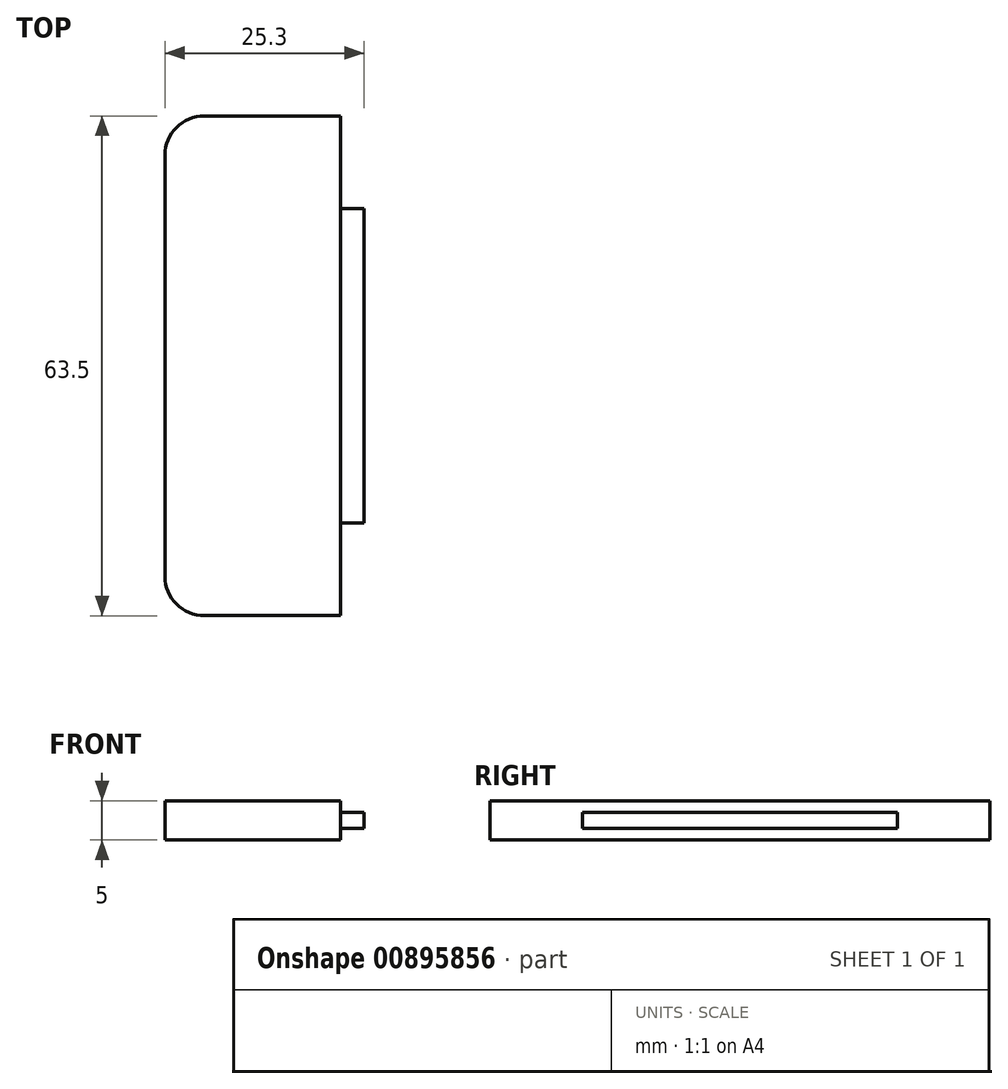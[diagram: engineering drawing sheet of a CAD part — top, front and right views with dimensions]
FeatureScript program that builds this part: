
annotation { "Feature Type Name" : "Feature", "Feature Type Description" : "" }
export const myFeature = defineFeature(function(context is Context, id is Id, definition is map)
    precondition{}
    {
        {
            var Q0;
            Q0=qCreatedBy(makeId("Right.planeOp"),FACE);
            var sketch = newSketch(context, id + "F0", { "sketchPlane" : qUnion([Q0])});
            skLineSegment(sketch, "E0.bottom", {"start": v(-31.75, 0) * mm, "end": v(31.75, 0) * mm});
            skLineSegment(sketch, "E0.top", {"start": v(-31.75, 5) * mm, "end": v(31.75, 5) * mm});
            skLineSegment(sketch, "E0.left", {"start": v(-31.75, 0) * mm, "end": v(-31.75, 5) * mm});
            skLineSegment(sketch, "E0.right", {"start": v(31.75, 0) * mm, "end": v(31.75, 5) * mm});
            skSolve(sketch);
        }
        {
            var Q0;
            Q0=makeQuery(id+"F0.imprint","IMPRINT",FACE,{"disambiguationData":[TD([[makeQuery(id+"F0.imprint","IMPRINT",EDGE,{"derivedFrom":sQuery(id+"F0.wireOp",EDGE,"E0.bottom")}),1.0]])]});
            extrude(context, id + "F1", {"entities" : qUnion([Q0]), "oppositeDirection" : true, "depth" : 22.3 * mm, "offsetDistance" : 25 * mm});
        }
        {
            var Q0;
            Q0=makeQuery(id+"F1.opExtrude","CAP_FACE",FACE,{"disambiguationData":[OSD([sQuery(id+"F0.wireOp",EDGE,"E0.bottom"),sQuery(id+"F0.wireOp",EDGE,"E0.top"),sQuery(id+"F0.wireOp",EDGE,"E0.left"),sQuery(id+"F0.wireOp",EDGE,"E0.right")])],"isStart":true});
            var sketch = newSketch(context, id + "F2", { "sketchPlane" : qUnion([Q0])});
            skLineSegment(sketch, "E1.bottom", {"start": v(-20, 1.5) * mm, "end": v(20, 1.5) * mm});
            skLineSegment(sketch, "E1.top", {"start": v(-20, 3.5) * mm, "end": v(20, 3.5) * mm});
            skLineSegment(sketch, "E1.left", {"start": v(-20, 1.5) * mm, "end": v(-20, 3.5) * mm});
            skLineSegment(sketch, "E1.right", {"start": v(20, 1.5) * mm, "end": v(20, 3.5) * mm});
            skPoint(sketch, "E1.middle", {"position": v(0, 2.5) * mm});
            skPoint(sketch, "E1.middle.positionSnap0", {"position": v(-31.75, 2.5) * mm});
            skPoint(sketch, "E1.middle.positionSnap1", {"position": v(0, 5) * mm});
            skPoint(sketch, "E1.centerSnap0", {"position": v(-31.75, 2.5) * mm});
            skPoint(sketch, "E1.centerSnap1", {"position": v(0, 5) * mm});
            skSolve(sketch);
        }
        {
            var Q0;
            Q0=qSketchRegion(id+"F2",true);
            extrude(context, id + "F3", {"entities" : qUnion([Q0]), "operationType" : NewBodyOperationType.ADD, "depth" : 3 * mm, "offsetDistance" : 25 * mm});
        }
        {
            var Q0;
            Q0=makeQuery(id+"F4.boolean.opBoolean","MERGE",EDGE,{"derivedFrom":[makeQuery(id+"F1.opExtrude","CAP_EDGE",EDGE,{"disambiguationData":[OSD([sQuery(id+"F0.wireOp",EDGE,"E0.left")])],"isStart":false}),makeQuery(id+"F4.opExtrude","SWEPT_EDGE",EDGE,{"disambiguationData":[OSD([sQuery(id+"FXh4Sg3UtugekUx_1.wireOp",EDGE,"Ubbl035J-z30R-Kqsf-Udrh-H0bbXLklV5ic"),sQuery(id+"FXh4Sg3UtugekUx_1.wireOp",EDGE,"MyniThw5-Nr24-tw2W-NILN-Vu69KHAhI73w")])]})]});
            var Q1;
            Q1=makeQuery(id+"F4.boolean.opBoolean","MERGE",EDGE,{"derivedFrom":[makeQuery(id+"F1.opExtrude","CAP_EDGE",EDGE,{"disambiguationData":[OSD([sQuery(id+"F0.wireOp",EDGE,"E0.right")])],"isStart":false}),makeQuery(id+"F4.opExtrude","SWEPT_EDGE",EDGE,{"disambiguationData":[OSD([sQuery(id+"FXh4Sg3UtugekUx_1.wireOp",EDGE,"RHjo1hUt-oSQh-2PV7-W0mQ-4d0R3KHODra4"),sQuery(id+"FXh4Sg3UtugekUx_1.wireOp",EDGE,"Ubbl035J-z30R-Kqsf-Udrh-H0bbXLklV5ic")])]})]});
            var Q2;
            Q2=makeQuery(id+"F4.opExtrude","SWEPT_EDGE",EDGE,{"disambiguationData":[OSD([sQuery(id+"FXh4Sg3UtugekUx_1.wireOp",EDGE,"mIeBr9P8-bOI6-yqE9-kVab-27R7m6AFeO5X"),sQuery(id+"FXh4Sg3UtugekUx_1.wireOp",EDGE,"0ZlcOWTk-LOnW-N0Od-jcdx-1FbijfS61vq5")])]});
            var Q3;
            Q3=makeQuery(id+"F4.opExtrude","SWEPT_EDGE",EDGE,{"disambiguationData":[OSD([sQuery(id+"FXh4Sg3UtugekUx_1.wireOp",EDGE,"gvjt3z26-lBGh-GkMT-igUa-fHP722nwAzBn"),sQuery(id+"FXh4Sg3UtugekUx_1.wireOp",EDGE,"mIeBr9P8-bOI6-yqE9-kVab-27R7m6AFeO5X")])]});
            fillet(context, id + "F5", {"entities" : qUnion([Q0, Q1, Q2, Q3]), "radius" : 5 * mm, "tangentPropagation" : true, "allowEdgeOverflow" : false});
        }
    });
